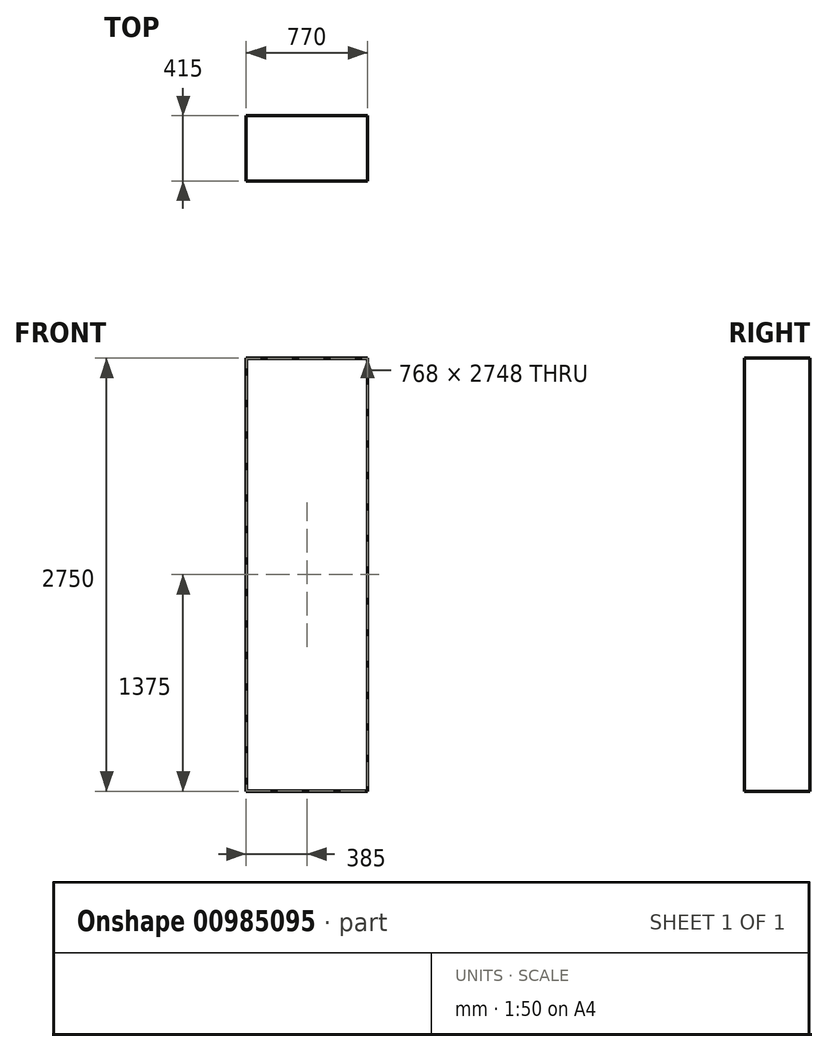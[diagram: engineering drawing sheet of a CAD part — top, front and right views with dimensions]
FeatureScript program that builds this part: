
annotation { "Feature Type Name" : "Feature", "Feature Type Description" : "" }
export const myFeature = defineFeature(function(context is Context, id is Id, definition is map)
    precondition{}
    {
        {
            var Q0;
            Q0=qCreatedBy(makeId("Front.planeOp"),FACE);
            var sketch = newSketch(context, id + "F0", { "sketchPlane" : qUnion([Q0])});
            skLineSegment(sketch, "E0.bottom", {"start": v(0, 0) * mm, "end": v(-770, 0) * mm});
            skLineSegment(sketch, "E0.top", {"start": v(0, 2750) * mm, "end": v(-770, 2750) * mm});
            skLineSegment(sketch, "E0.left", {"start": v(0, 0) * mm, "end": v(0, 2750) * mm});
            skLineSegment(sketch, "E0.right", {"start": v(-770, 0) * mm, "end": v(-770, 2750) * mm});
            skSolve(sketch);
        }
        {
            var Q0;
            Q0 = qSketchRegion(id + "F0", true);
            extrude(context, id + "F1", {"entities" : qUnion([Q0]), "depth" : 415 * mm, "offsetDistance" : 25.4 * mm});
        }
        {
            var Q0;
            Q0=makeQuery(id+"F1.opExtrude","CAP_FACE",FACE,{"disambiguationData":[OSD([sQuery(id+"F0.wireOp",EDGE,"E0.bottom"),sQuery(id+"F0.wireOp",EDGE,"E0.top"),sQuery(id+"F0.wireOp",EDGE,"E0.left"),sQuery(id+"F0.wireOp",EDGE,"E0.right")])],"isStart":false});
            var Q1;
            Q1=makeQuery(id+"F1.opExtrude","CAP_FACE",FACE,{"disambiguationData":[OSD([sQuery(id+"F0.wireOp",EDGE,"E0.bottom"),sQuery(id+"F0.wireOp",EDGE,"E0.top"),sQuery(id+"F0.wireOp",EDGE,"E0.left"),sQuery(id+"F0.wireOp",EDGE,"E0.right")])],"isStart":true});
            shell(context, id + "F2", {"entities" : qUnion([Q0, Q1]), "thickness" : 1 * mm});
        }
    });
